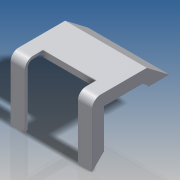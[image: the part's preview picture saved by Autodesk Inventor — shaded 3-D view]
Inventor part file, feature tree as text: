
AUTODESK INVENTOR PART (.ipt)
format: ipt  version: 2016 SP2 (Build 200236200, 236)  size: 325,632 bytes
history: native  units: in
note: dims shown in document units (in); Inventor stores cm internally (conversion verified against a paired STEP export)
features: extrude x5, sketch x2, mirror x1, fillet x1
ambient origin geometry x8: Origin, YZ Plane, XZ Plane, XY Plane, X Axis, Y Axis, Z Axis, Center Point
bodies: Solid1 (feature_tree)
feature tree (9):
  sketch  "Sketch2"  dims[d0=0.2047in d1=1.1024in]
  extrude  "Extrusion1"  Depth=1.1024in
  extrude  "Extrusion2"  Depth=1.3386in
  extrude  "Extrusion3"  Depth=0.0039in
  extrude  "Extrusion4"  Depth=0.0039in
  extrude  "Extrusion5"  TaperAngle=45.0deg  [1 undecoded]
  mirror  "Mirror1"
  fillet  "Fillet1"  Radius=0.0157in
  sketch  "Sketch3"  dims[d2=0.2047in d3=1.3386in d4=0.9449in d5=0.1417in d6=45.0deg d7=0.0157in d8=0.2992in d9=0.315in d10=0.9921in d11=0.0472in d12=0.0472in d13=0.315in d14=0.063in d15=0.0472in d16=1.4173in d17=0.0in d18=1.3228in d19=0.0in d20=0.9134in d21=0.0in d22=0.9134in d23=0.0in d24=0.0157in d25=0.0157in d26=0.0in d27=0.0039in]
note: 1 required parameter value undecoded (feature->parameter linkage not recoverable at this tier; creation-order binding heuristic only, values carry confidence <= 0.55)
